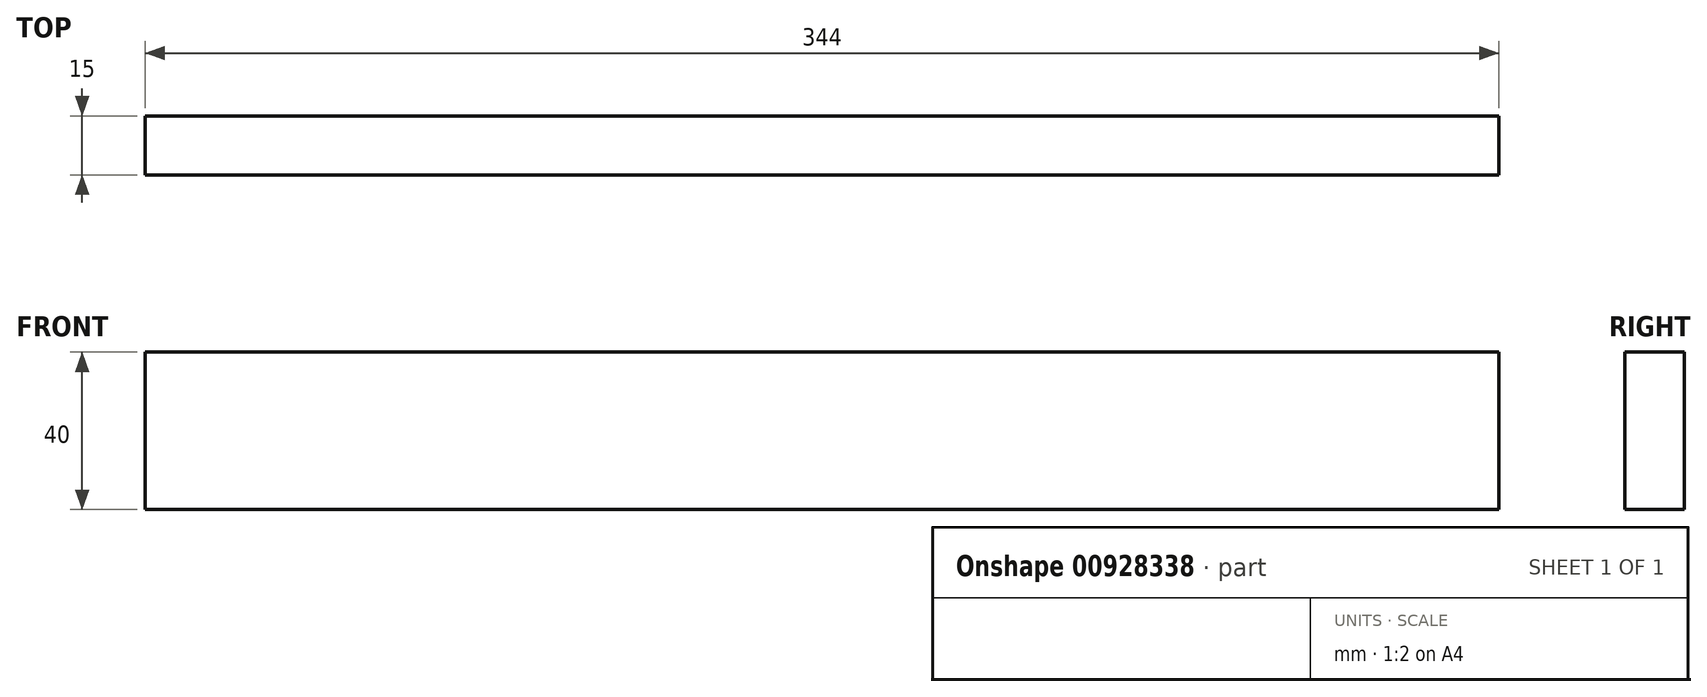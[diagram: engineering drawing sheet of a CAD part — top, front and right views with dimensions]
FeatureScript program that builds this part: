
annotation { "Feature Type Name" : "Feature", "Feature Type Description" : "" }
export const myFeature = defineFeature(function(context is Context, id is Id, definition is map)
    precondition{}
    {
        {
            var Q0;
            Q0=qCreatedBy(makeId("Top.planeOp"),FACE);
            var sketch = newSketch(context, id + "F0", { "sketchPlane" : qUnion([Q0])});
            skLineSegment(sketch, "E0.bottom", {"start": v(172, 7.5) * mm, "end": v(-172, 7.5) * mm});
            skLineSegment(sketch, "E0.top", {"start": v(172, -7.5) * mm, "end": v(-172, -7.5) * mm});
            skLineSegment(sketch, "E0.left", {"start": v(172, 7.5) * mm, "end": v(172, -7.5) * mm});
            skLineSegment(sketch, "E0.right", {"start": v(-172, 7.5) * mm, "end": v(-172, -7.5) * mm});
            skPoint(sketch, "E0.middle", {"position": v(0, 0) * mm});
            skSolve(sketch);
        }
        {
            var Q0;
            Q0=makeQuery(id+"F0.imprint","IMPRINT",FACE,{"disambiguationData":[TD([[makeQuery(id+"F0.imprint","IMPRINT",EDGE,{"derivedFrom":sQuery(id+"F0.wireOp",EDGE,"E0.bottom")}),1.0]])]});
            extrude(context, id + "F1", {"entities" : qUnion([Q0]), "depth" : -40 * mm, "offsetDistance" : 25 * mm});
        }
    });
